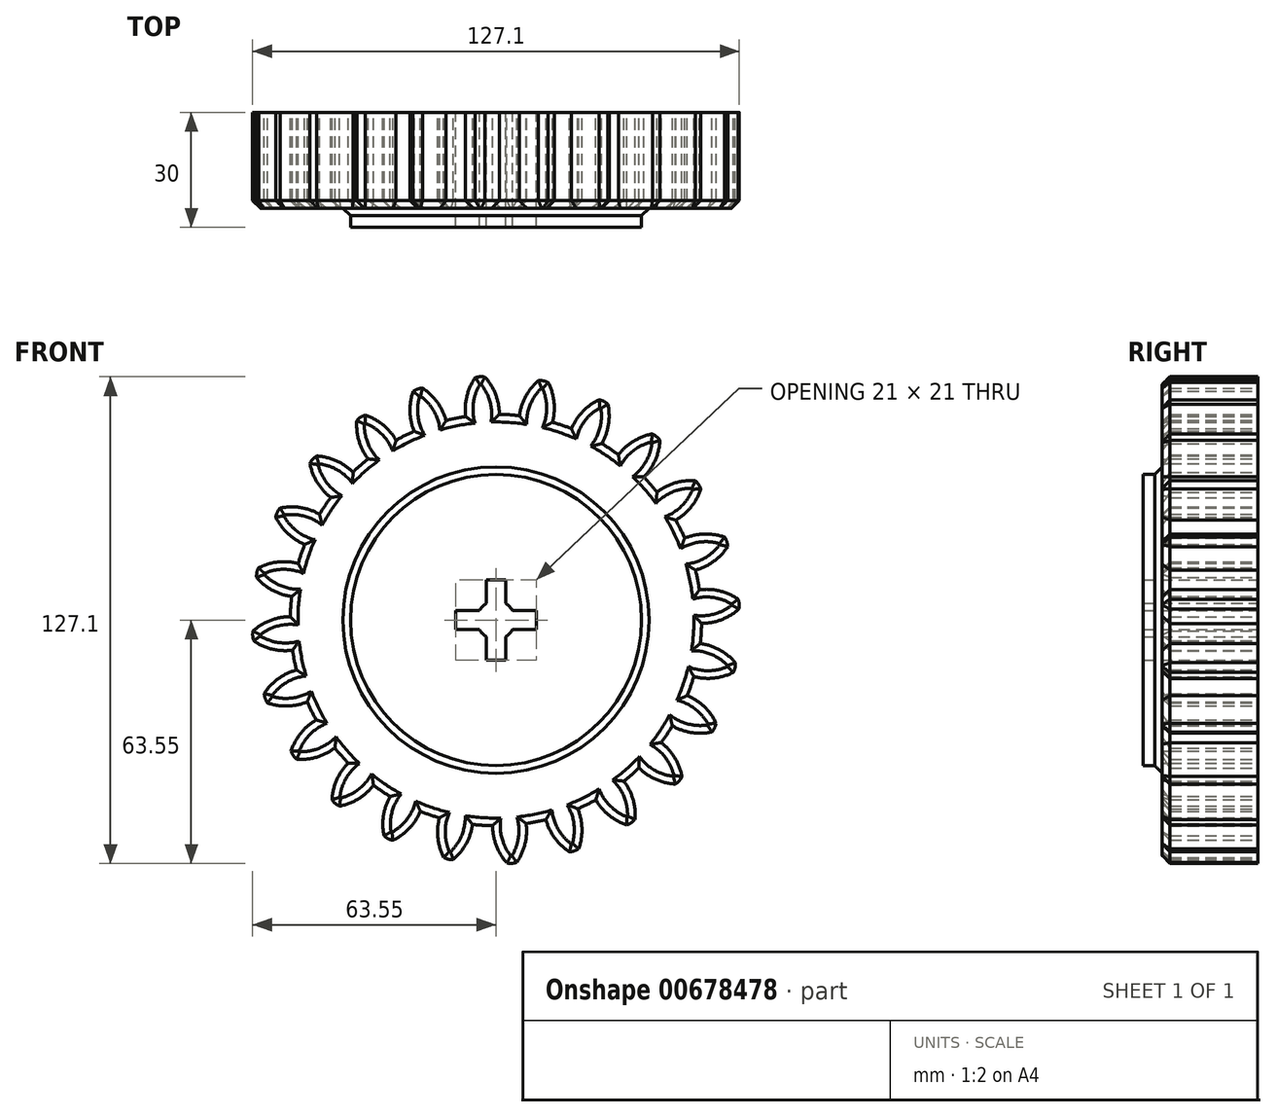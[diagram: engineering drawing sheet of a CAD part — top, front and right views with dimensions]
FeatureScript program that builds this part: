
annotation { "Feature Type Name" : "Feature", "Feature Type Description" : "" }
export const myFeature = defineFeature(function(context is Context, id is Id, definition is map)
    precondition{}
    {
        {
            var Q0;
            Q0=qCreatedBy(makeId("Front.planeOp"),FACE);
            var sketch = newSketch(context, id + "F0", { "sketchPlane" : qUnion([Q0])});
            skCircle(sketch, "E0", {"center": v(0, 0) * mm, "radius": 53.72 * mm});
            skCircle(sketch, "E1", {"center": v(0, 0) * mm, "radius": 58.67 * mm, "construction": true});
            skCircle(sketch, "E2", {"center": v(0, 0) * mm, "radius": 63.5 * mm, "construction": true});
            skLineSegment(sketch, "E3", {"start": v(0, 0) * mm, "end": v(0, 101.5) * mm, "construction": true});
            skLineSegment(sketch, "E4", {"start": v(0, 0) * mm, "end": v(-7.23, 110.28) * mm, "construction": true});
            skLineSegment(sketch, "E5", {"start": v(0, 58.67) * mm, "end": v(-75.03, 58.67) * mm, "construction": true});
            skLineSegment(sketch, "E6", {"start": v(0, 58.67) * mm, "end": v(-75.24, 31.29) * mm, "construction": true});
            skCircle(sketch, "E7", {"center": v(0, 0) * mm, "radius": 55.14 * mm, "construction": true});
            skCircle(sketch, "E8", {"center": v(0, 58.67) * mm, "radius": 14.6 * mm, "construction": true});
            skCircle(sketch, "E9", {"center": v(-13.72, 53.68) * mm, "radius": 14.6 * mm, "construction": true});
            skArc(sketch, "E10", {"start": v(0, 58.67) * mm, "mid": v(-1.2, 61.2) * mm, "end": v(-2.86, 63.44) * mm});
            skArc(sketch, "E11", {"start": v(0.88, 53.71) * mm, "mid": v(0.66, 56.23) * mm, "end": v(0, 58.67) * mm});
            skArc(sketch, "E12.MirrorCS", {"start": v(-7.66, 58.17) * mm, "mid": v(-6.8, 60.82) * mm, "end": v(-5.45, 63.27) * mm});
            skArc(sketch, "E13.MirrorCS", {"start": v(-7.88, 53.14) * mm, "mid": v(-8, 55.67) * mm, "end": v(-7.66, 58.17) * mm});
            skArc(sketch, "E14", {"start": v(-2.86, 63.44) * mm, "mid": v(-4.16, 63.54) * mm, "end": v(-5.45, 63.27) * mm});
            skCircle(sketch, "E15", {"center": v(0, 0) * mm, "radius": 38 * mm});
            skLineSegment(sketch, "E16.bottom", {"start": v(-2.5, -10.5) * mm, "end": v(2.5, -10.5) * mm});
            skLineSegment(sketch, "E16.top", {"start": v(-2.5, 10.5) * mm, "end": v(2.5, 10.5) * mm});
            skLineSegment(sketch, "E16.left", {"start": v(-2.5, -10.5) * mm, "end": v(-2.5, 10.5) * mm});
            skLineSegment(sketch, "E16.right", {"start": v(2.5, -10.5) * mm, "end": v(2.5, 10.5) * mm});
            skLineSegment(sketch, "E17.bottom", {"start": v(-10.5, -2.5) * mm, "end": v(10.5, -2.5) * mm});
            skLineSegment(sketch, "E17.top", {"start": v(-10.5, 2.5) * mm, "end": v(10.5, 2.5) * mm});
            skLineSegment(sketch, "E17.left", {"start": v(-10.5, -2.5) * mm, "end": v(-10.5, 2.5) * mm});
            skLineSegment(sketch, "E17.right", {"start": v(10.5, -2.5) * mm, "end": v(10.5, 2.5) * mm});
            skCircle(sketch, "E18", {"center": v(0, 0) * mm, "radius": 5 * mm});
            skSolve(sketch);
        }
        {
            var Q0;
            {var subQ0=sQuery(id+"F0.wireOp",EDGE,"E0");var subQ1=makeQuery(id+"F0.imprint","INTERSECT",VERTEX,{"derivedFrom":[subQ0,sQuery(id+"F0.wireOp",EDGE,"E11")]});Q0=makeQuery(id+"F0.imprint","IMPRINT",FACE,{"disambiguationData":[TD([[makeQuery(id+"F0.imprint","IMPRINT",EDGE,{"disambiguationData":[TD([[subQ1,-1.0]])],"derivedFrom":subQ0}),1.0]])]});}
            var Q1;
            Q1=makeQuery(id+"F0.imprint","IMPRINT",FACE,{"disambiguationData":[TD([[makeQuery(id+"F0.imprint","IMPRINT",EDGE,{"derivedFrom":sQuery(id+"F0.wireOp",EDGE,"E10")}),1.0]])]});
            extrude(context, id + "F1", {"entities" : qUnion([Q0, Q1]), "depth" : 25 * mm, "offsetDistance" : 25 * mm});
        }
        {
            var Q0;
            Q0=makeQuery(id+"F1.opExtrude","SWEPT_BODY",BODY,{"disambiguationData":[OSD([sQuery(id+"F0.wireOp",EDGE,"E0"),sQuery(id+"F0.wireOp",EDGE,"E10"),sQuery(id+"F0.wireOp",EDGE,"E11"),sQuery(id+"F0.wireOp",EDGE,"E12.MirrorCS"),sQuery(id+"F0.wireOp",EDGE,"E13.MirrorCS"),sQuery(id+"F0.wireOp",EDGE,"E14")])]});
            var Q1;
            Q1=makeQuery(id+"F1.opExtrude","SWEPT_FACE",FACE,{"disambiguationData":[OSD([sQuery(id+"F0.wireOp",EDGE,"E0")])]});
            circularPattern(context, id + "F2", {"entities" : qUnion([Q0]), "axis" : qUnion([Q1]), "angle" : 360 * degree, "instanceCount" : 24, "equalSpace" : true});
        }
        {
            var Q0;
            Q0=makeQuery(id+"F0.imprint","IMPRINT",FACE,{"disambiguationData":[TD([[makeQuery(id+"F0.imprint","IMPRINT",EDGE,{"derivedFrom":sQuery(id+"F0.wireOp",EDGE,"E15")}),1.0]])]});
            extrude(context, id + "F3", {"entities" : qUnion([Q0]), "operationType" : NewBodyOperationType.ADD, "depth" : 30 * mm, "offsetDistance" : 25 * mm});
        }
        {
            var Q0;
            {var subQ0=makeQuery(id+"F1.opExtrude","CAP_FACE",FACE,{"disambiguationData":[OSD([sQuery(id+"F0.wireOp",EDGE,"E0"),sQuery(id+"F0.wireOp",EDGE,"E10"),sQuery(id+"F0.wireOp",EDGE,"E11"),sQuery(id+"F0.wireOp",EDGE,"E12.MirrorCS"),sQuery(id+"F0.wireOp",EDGE,"E13.MirrorCS"),sQuery(id+"F0.wireOp",EDGE,"E14"),sQuery(id+"F0.wireOp",EDGE,"E15")])],"isStart":false});Q0=makeQuery(id+"F3.boolean.opBoolean","MERGE",FACE,{"derivedFrom":[subQ0,makeQuery(id+"F2.opPattern","COPY",FACE,{"derivedFrom":subQ0,"instanceName":"1"}),makeQuery(id+"F2.opPattern","COPY",FACE,{"derivedFrom":subQ0,"instanceName":"2"}),makeQuery(id+"F2.opPattern","COPY",FACE,{"derivedFrom":subQ0,"instanceName":"3"}),makeQuery(id+"F2.opPattern","COPY",FACE,{"derivedFrom":subQ0,"instanceName":"4"}),makeQuery(id+"F2.opPattern","COPY",FACE,{"derivedFrom":subQ0,"instanceName":"5"}),makeQuery(id+"F2.opPattern","COPY",FACE,{"derivedFrom":subQ0,"instanceName":"6"}),makeQuery(id+"F2.opPattern","COPY",FACE,{"derivedFrom":subQ0,"instanceName":"7"}),makeQuery(id+"F2.opPattern","COPY",FACE,{"derivedFrom":subQ0,"instanceName":"8"}),makeQuery(id+"F2.opPattern","COPY",FACE,{"derivedFrom":subQ0,"instanceName":"9"}),makeQuery(id+"F2.opPattern","COPY",FACE,{"derivedFrom":subQ0,"instanceName":"10"}),makeQuery(id+"F2.opPattern","COPY",FACE,{"derivedFrom":subQ0,"instanceName":"11"}),makeQuery(id+"F2.opPattern","COPY",FACE,{"derivedFrom":subQ0,"instanceName":"12"}),makeQuery(id+"F2.opPattern","COPY",FACE,{"derivedFrom":subQ0,"instanceName":"13"}),makeQuery(id+"F2.opPattern","COPY",FACE,{"derivedFrom":subQ0,"instanceName":"14"}),makeQuery(id+"F2.opPattern","COPY",FACE,{"derivedFrom":subQ0,"instanceName":"15"}),makeQuery(id+"F2.opPattern","COPY",FACE,{"derivedFrom":subQ0,"instanceName":"16"}),makeQuery(id+"F2.opPattern","COPY",FACE,{"derivedFrom":subQ0,"instanceName":"17"}),makeQuery(id+"F2.opPattern","COPY",FACE,{"derivedFrom":subQ0,"instanceName":"18"}),makeQuery(id+"F2.opPattern","COPY",FACE,{"derivedFrom":subQ0,"instanceName":"19"}),makeQuery(id+"F2.opPattern","COPY",FACE,{"derivedFrom":subQ0,"instanceName":"20"}),makeQuery(id+"F2.opPattern","COPY",FACE,{"derivedFrom":subQ0,"instanceName":"21"}),makeQuery(id+"F2.opPattern","COPY",FACE,{"derivedFrom":subQ0,"instanceName":"22"}),makeQuery(id+"F2.opPattern","COPY",FACE,{"derivedFrom":subQ0,"instanceName":"23"})]});}
            chamfer(context, id + "F4", {"entities" : qUnion([Q0]), "width" : 2 * mm, "tangentPropagation" : true});
        }
    });
